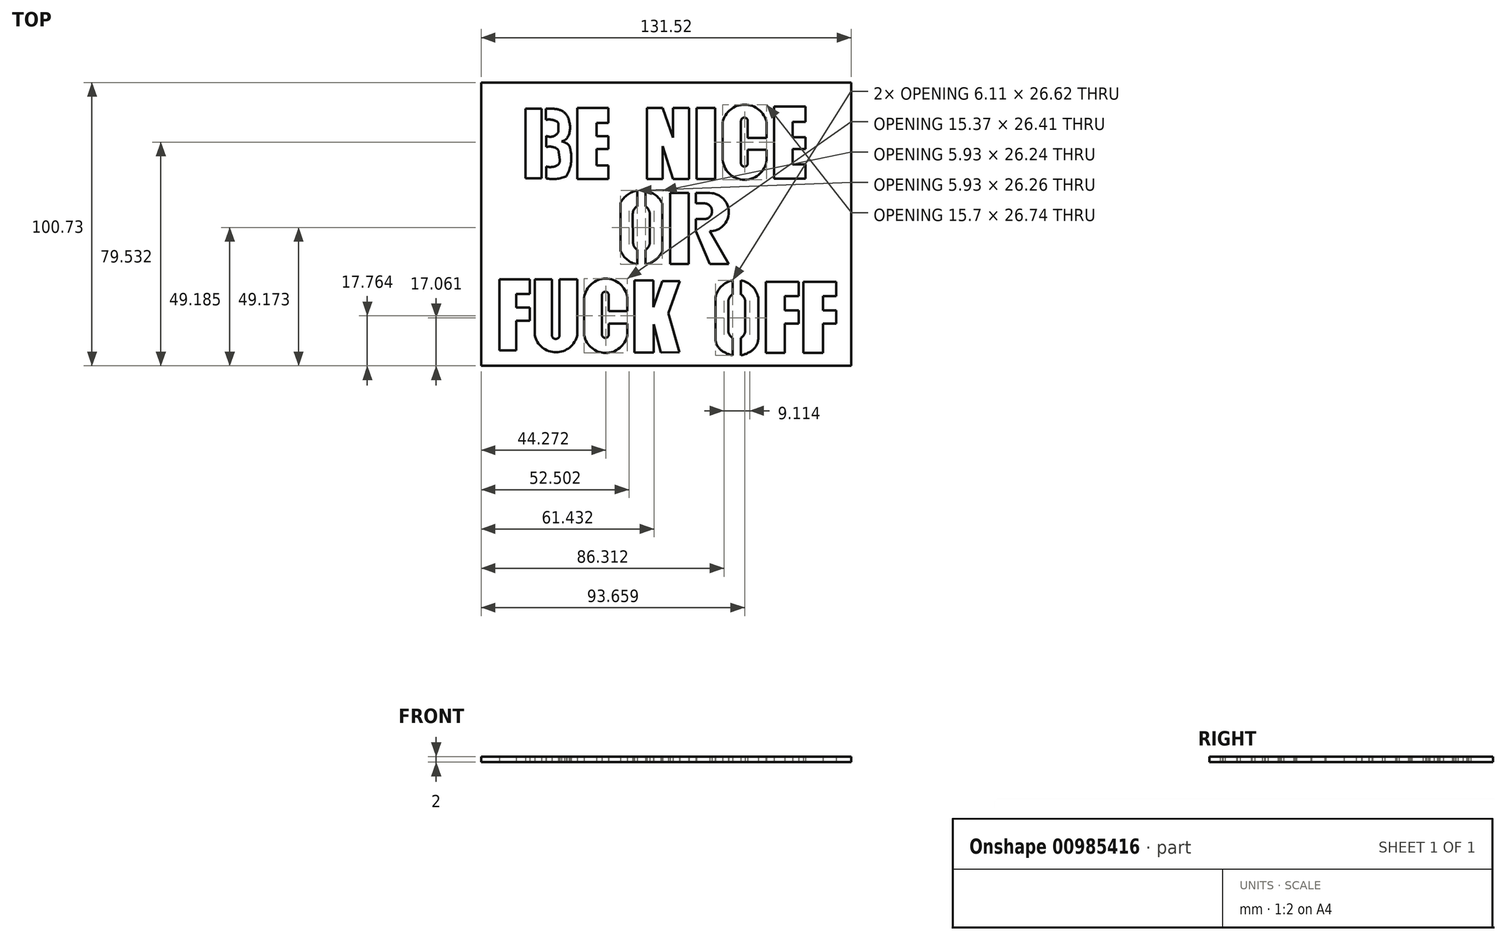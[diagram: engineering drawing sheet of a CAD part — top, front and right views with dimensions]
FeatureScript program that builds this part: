
annotation { "Feature Type Name" : "Feature", "Feature Type Description" : "" }
export const myFeature = defineFeature(function(context is Context, id is Id, definition is map)
    precondition{}
    {
        {
            var Q0;
            Q0=qCreatedBy(makeId("Top.planeOp"),FACE);
            var sketch = newSketch(context, id + "F0", { "sketchPlane" : qUnion([Q0])});
            skLineSegment(sketch, "E0", {"start": v(-58.34, 79.54) * mm, "end": v(-58.34, 83.48) * mm});
            skLineSegment(sketch, "E1", {"start": v(-58.22, 73.86) * mm, "end": v(-58.22, 69.88) * mm});
            skLineSegment(sketch, "E2", {"start": v(-58.22, 62.97) * mm, "end": v(-58.22, 58.7) * mm});
            skLineSegment(sketch, "E3", {"start": v(-58.34, 83.48) * mm, "end": v(-55.71, 83.48) * mm});
            skArc(sketch, "E4", {"start": v(-51.69, 82.15) * mm, "mid": v(-53.6, 83.14) * mm, "end": v(-55.71, 83.48) * mm});
            skArc(sketch, "E5", {"start": v(-50, 78.93) * mm, "mid": v(-50.58, 80.68) * mm, "end": v(-51.69, 82.15) * mm});
            skArc(sketch, "E6", {"start": v(-50.76, 73) * mm, "mid": v(-49.75, 75.89) * mm, "end": v(-50, 78.93) * mm});
            skArc(sketch, "E7", {"start": v(-52.7, 71.92) * mm, "mid": v(-51.63, 72.3) * mm, "end": v(-50.76, 73) * mm});
            skArc(sketch, "E8", {"start": v(-50, 70.42) * mm, "mid": v(-51.23, 71.38) * mm, "end": v(-52.7, 71.92) * mm});
            skArc(sketch, "E9", {"start": v(-49.42, 68) * mm, "mid": v(-49.63, 69.23) * mm, "end": v(-50, 70.42) * mm});
            skArc(sketch, "E10", {"start": v(-58.22, 58.7) * mm, "mid": v(-54.62, 58.57) * mm, "end": v(-51.12, 59.44) * mm});
            skArc(sketch, "E11", {"start": v(-51.12, 59.44) * mm, "mid": v(-49.47, 63.56) * mm, "end": v(-49.42, 68) * mm});
            skLineSegment(sketch, "E12", {"start": v(-47.15, 58.57) * mm, "end": v(-47.15, 83.76) * mm});
            skPoint(sketch, "E12.startSnap0", {"position": v(-54.62, 58.57) * mm});
            skLineSegment(sketch, "E13", {"start": v(-47.15, 83.76) * mm, "end": v(-36.04, 83.76) * mm});
            skLineSegment(sketch, "E14", {"start": v(-36.04, 83.76) * mm, "end": v(-36.04, 78.4) * mm});
            skLineSegment(sketch, "E15", {"start": v(-36.04, 78.4) * mm, "end": v(-40.33, 78.4) * mm});
            skLineSegment(sketch, "E16", {"start": v(-40.33, 78.4) * mm, "end": v(-40.33, 73.8) * mm});
            skLineSegment(sketch, "E17", {"start": v(-40.33, 73.8) * mm, "end": v(-36.04, 73.8) * mm});
            skLineSegment(sketch, "E18", {"start": v(-36.04, 73.8) * mm, "end": v(-36.04, 69.2) * mm});
            skLineSegment(sketch, "E19", {"start": v(-36.04, 69.2) * mm, "end": v(-40.33, 69.2) * mm});
            skLineSegment(sketch, "E20", {"start": v(-40.33, 69.2) * mm, "end": v(-40.33, 63.38) * mm});
            skLineSegment(sketch, "E21", {"start": v(-40.33, 63.38) * mm, "end": v(-36.04, 63.38) * mm});
            skLineSegment(sketch, "E22", {"start": v(-36.04, 63.38) * mm, "end": v(-36.04, 58.57) * mm});
            skLineSegment(sketch, "E23", {"start": v(-36.04, 58.57) * mm, "end": v(-47.15, 58.57) * mm});
            skLineSegment(sketch, "E24", {"start": v(-22.3, 58.57) * mm, "end": v(-22.3, 83.76) * mm});
            skLineSegment(sketch, "E25", {"start": v(-22.3, 83.76) * mm, "end": v(-16.73, 83.76) * mm});
            skLineSegment(sketch, "E26", {"start": v(-16.73, 83.76) * mm, "end": v(-13.1, 73.2) * mm});
            skLineSegment(sketch, "E27", {"start": v(-13.1, 73.2) * mm, "end": v(-13.1, 83.76) * mm});
            skLineSegment(sketch, "E28", {"start": v(-13.1, 83.76) * mm, "end": v(-7.43, 83.76) * mm});
            skLineSegment(sketch, "E29", {"start": v(-7.43, 83.76) * mm, "end": v(-7.43, 58.57) * mm});
            skLineSegment(sketch, "E30", {"start": v(-7.43, 58.57) * mm, "end": v(-13.1, 58.57) * mm});
            skLineSegment(sketch, "E31", {"start": v(-13.1, 58.57) * mm, "end": v(-16.73, 70.13) * mm});
            skLineSegment(sketch, "E32", {"start": v(-16.73, 70.13) * mm, "end": v(-16.73, 58.57) * mm});
            skLineSegment(sketch, "E33", {"start": v(-16.73, 58.57) * mm, "end": v(-22.3, 58.57) * mm});
            skLineSegment(sketch, "E34.bottom", {"start": v(-4.73, 83.76) * mm, "end": v(1.9, 83.76) * mm});
            skLineSegment(sketch, "E34.top", {"start": v(-4.73, 58.57) * mm, "end": v(1.9, 58.57) * mm});
            skLineSegment(sketch, "E34.left", {"start": v(-4.73, 83.76) * mm, "end": v(-4.73, 58.57) * mm});
            skLineSegment(sketch, "E34.right", {"start": v(1.9, 83.76) * mm, "end": v(1.9, 58.57) * mm});
            skLineSegment(sketch, "E35", {"start": v(4.53, 78.6) * mm, "end": v(4.53, 66.08) * mm});
            skLineSegment(sketch, "E36", {"start": v(11.08, 64.14) * mm, "end": v(11.08, 79.13) * mm});
            skLineSegment(sketch, "E37", {"start": v(13.5, 73.1) * mm, "end": v(13.5, 79.13) * mm});
            skLineSegment(sketch, "E38", {"start": v(13.5, 68.86) * mm, "end": v(13.5, 64.08) * mm});
            skArc(sketch, "E39", {"start": v(13.5, 79.13) * mm, "mid": v(12.3, 80.34) * mm, "end": v(11.08, 79.13) * mm});
            skArc(sketch, "E40", {"start": v(11.08, 64.14) * mm, "mid": v(12.26, 62.93) * mm, "end": v(13.5, 64.08) * mm});
            skLineSegment(sketch, "E41", {"start": v(13.5, 68.86) * mm, "end": v(20.23, 68.86) * mm});
            skLineSegment(sketch, "E42", {"start": v(13.5, 73.1) * mm, "end": v(20.23, 73.1) * mm});
            skLineSegment(sketch, "E43", {"start": v(20.23, 73.1) * mm, "end": v(20.23, 78.6) * mm});
            skLineSegment(sketch, "E44", {"start": v(20.23, 68.86) * mm, "end": v(20.23, 66.08) * mm});
            skArc(sketch, "E45", {"start": v(4.53, 66.08) * mm, "mid": v(12.38, 58.23) * mm, "end": v(20.23, 66.08) * mm});
            skArc(sketch, "E46", {"start": v(20.23, 78.6) * mm, "mid": v(12.38, 84.97) * mm, "end": v(4.53, 78.6) * mm});
            skLineSegment(sketch, "E47", {"start": v(22.87, 58.64) * mm, "end": v(22.87, 84.24) * mm});
            skLineSegment(sketch, "E48", {"start": v(22.87, 84.24) * mm, "end": v(34.02, 84.24) * mm});
            skLineSegment(sketch, "E49", {"start": v(34.02, 84.24) * mm, "end": v(34.02, 78.84) * mm});
            skLineSegment(sketch, "E50", {"start": v(34.02, 78.84) * mm, "end": v(29.45, 78.84) * mm});
            skLineSegment(sketch, "E51", {"start": v(29.45, 78.84) * mm, "end": v(29.45, 73.36) * mm});
            skLineSegment(sketch, "E52", {"start": v(29.45, 73.36) * mm, "end": v(34.02, 73.36) * mm});
            skLineSegment(sketch, "E53", {"start": v(34.02, 73.36) * mm, "end": v(34.02, 69.15) * mm});
            skLineSegment(sketch, "E54", {"start": v(34.02, 69.15) * mm, "end": v(29.45, 69.15) * mm});
            skLineSegment(sketch, "E55", {"start": v(29.45, 69.15) * mm, "end": v(29.45, 63.76) * mm});
            skLineSegment(sketch, "E56", {"start": v(29.45, 63.76) * mm, "end": v(34.02, 63.76) * mm});
            skLineSegment(sketch, "E57", {"start": v(34.02, 63.76) * mm, "end": v(34.02, 58.64) * mm});
            skLineSegment(sketch, "E58", {"start": v(34.02, 58.64) * mm, "end": v(22.87, 58.64) * mm});
            skArc(sketch, "E59", {"start": v(-16.88, 49.84) * mm, "mid": v(-19.32, 52.8) * mm, "end": v(-22.81, 54.36) * mm});
            skArc(sketch, "E60", {"start": v(-31.74, 33) * mm, "mid": v(-29.4, 29.8) * mm, "end": v(-25.81, 28.12) * mm});
            skLineSegment(sketch, "E61", {"start": v(-16.88, 33) * mm, "end": v(-16.88, 49.84) * mm});
            skLineSegment(sketch, "E62", {"start": v(-31.74, 50.12) * mm, "end": v(-31.74, 33) * mm});
            skArc(sketch, "E63.trimOffspring", {"start": v(-25.81, 54.39) * mm, "mid": v(-29.27, 52.93) * mm, "end": v(-31.74, 50.12) * mm});
            skArc(sketch, "E64.trimOffspring", {"start": v(-22.81, 28.12) * mm, "mid": v(-19.23, 29.8) * mm, "end": v(-16.88, 33) * mm});
            skLineSegment(sketch, "E65", {"start": v(-14.14, 53.5) * mm, "end": v(-14.14, 28.29) * mm});
            skLineSegment(sketch, "E66", {"start": v(-14.14, 28.29) * mm, "end": v(-7.48, 28.29) * mm});
            skLineSegment(sketch, "E67", {"start": v(-7.48, 28.29) * mm, "end": v(-7.48, 39.95) * mm});
            skPoint(sketch, "E68.orphan", {"position": v(-14.14, 54.5) * mm});
            skLineSegment(sketch, "E69", {"start": v(-7.48, 43.75) * mm, "end": v(-7.48, 49.61) * mm});
            skLineSegment(sketch, "E70", {"start": v(-7.48, 49.61) * mm, "end": v(-7.48, 53.5) * mm});
            skLineSegment(sketch, "E71.trimOffspring", {"start": v(-7.48, 53.5) * mm, "end": v(-14.14, 53.5) * mm});
            skLineSegment(sketch, "E72", {"start": v(-74.78, -2.43) * mm, "end": v(-74.78, 22.79) * mm});
            skLineSegment(sketch, "E73", {"start": v(-74.78, 22.79) * mm, "end": v(-63.97, 22.79) * mm});
            skLineSegment(sketch, "E74", {"start": v(-63.97, 22.79) * mm, "end": v(-63.97, 17.56) * mm});
            skLineSegment(sketch, "E75", {"start": v(-63.97, 17.56) * mm, "end": v(-68.85, 17.56) * mm});
            skLineSegment(sketch, "E76", {"start": v(-68.85, 17.56) * mm, "end": v(-68.85, 12.8) * mm});
            skLineSegment(sketch, "E77", {"start": v(-68.85, 12.8) * mm, "end": v(-64.06, 12.8) * mm});
            skLineSegment(sketch, "E78", {"start": v(-64.06, 12.8) * mm, "end": v(-64.06, 8.1) * mm});
            skLineSegment(sketch, "E79", {"start": v(-64.06, 8.1) * mm, "end": v(-68.85, 8.1) * mm});
            skLineSegment(sketch, "E80", {"start": v(-68.85, 8.1) * mm, "end": v(-68.85, -2.43) * mm});
            skLineSegment(sketch, "E81", {"start": v(-68.85, -2.43) * mm, "end": v(-74.78, -2.43) * mm});
            skLineSegment(sketch, "E82", {"start": v(-62.3, 22.76) * mm, "end": v(-56.19, 22.76) * mm});
            skLineSegment(sketch, "E83", {"start": v(-62.3, 22.76) * mm, "end": v(-62.3, 3) * mm});
            skLineSegment(sketch, "E84", {"start": v(-56.19, 22.76) * mm, "end": v(-56.19, 3) * mm});
            skLineSegment(sketch, "E85", {"start": v(-53.43, 22.76) * mm, "end": v(-53.43, 3) * mm});
            skLineSegment(sketch, "E86", {"start": v(-53.43, 22.76) * mm, "end": v(-47.1, 22.76) * mm});
            skLineSegment(sketch, "E87", {"start": v(-47.1, 22.76) * mm, "end": v(-47.1, 3) * mm});
            skArc(sketch, "E88", {"start": v(-56.19, 3) * mm, "mid": v(-54.8, 1.61) * mm, "end": v(-53.43, 3) * mm});
            skArc(sketch, "E89", {"start": v(-62.3, 3) * mm, "mid": v(-54.7, -3.12) * mm, "end": v(-47.1, 3) * mm});
            skLineSegment(sketch, "E90", {"start": v(-35.93, 11.56) * mm, "end": v(-29.34, 11.56) * mm});
            skLineSegment(sketch, "E91", {"start": v(-29.34, 7.1) * mm, "end": v(-35.93, 7.1) * mm});
            skLineSegment(sketch, "E92", {"start": v(-35.93, 7.1) * mm, "end": v(-35.93, 3.16) * mm});
            skLineSegment(sketch, "E93", {"start": v(-38.33, 3.16) * mm, "end": v(-38.33, 17.21) * mm});
            skLineSegment(sketch, "E94", {"start": v(-35.93, 11.56) * mm, "end": v(-35.93, 17.21) * mm});
            skArc(sketch, "E95", {"start": v(-35.93, 17.21) * mm, "mid": v(-37.13, 18.41) * mm, "end": v(-38.33, 17.21) * mm});
            skArc(sketch, "E96", {"start": v(-38.33, 3.16) * mm, "mid": v(-37.13, 1.96) * mm, "end": v(-35.93, 3.16) * mm});
            skLineSegment(sketch, "E97", {"start": v(-29.34, 7.1) * mm, "end": v(-29.34, 2.87) * mm});
            skLineSegment(sketch, "E98", {"start": v(-44.7, 2.87) * mm, "end": v(-44.7, 16.38) * mm});
            skArc(sketch, "E99", {"start": v(-29.32, 16.38) * mm, "mid": v(-37, 23.04) * mm, "end": v(-44.7, 16.38) * mm});
            skArc(sketch, "E100", {"start": v(-44.7, 2.87) * mm, "mid": v(-37.02, -3.37) * mm, "end": v(-29.34, 2.87) * mm});
            skLineSegment(sketch, "E101", {"start": v(-29.32, 16.38) * mm, "end": v(-29.34, 11.56) * mm});
            skLineSegment(sketch, "E102", {"start": v(-26.83, -3.2) * mm, "end": v(-26.83, 22.4) * mm});
            skLineSegment(sketch, "E103", {"start": v(-26.83, 22.4) * mm, "end": v(-20.13, 22.4) * mm});
            skLineSegment(sketch, "E104", {"start": v(-20.13, 22.4) * mm, "end": v(-20.13, 12.86) * mm});
            skLineSegment(sketch, "E105", {"start": v(-20.13, 12.86) * mm, "end": v(-16.95, 22.22) * mm});
            skLineSegment(sketch, "E106", {"start": v(-16.95, 22.22) * mm, "end": v(-10.68, 22.22) * mm});
            skLineSegment(sketch, "E107", {"start": v(-10.68, 22.22) * mm, "end": v(-14.8, 10.8) * mm});
            skLineSegment(sketch, "E108", {"start": v(-14.8, 10.8) * mm, "end": v(-10.77, -3.11) * mm});
            skLineSegment(sketch, "E109", {"start": v(-10.77, -3.11) * mm, "end": v(-17.47, -3.18) * mm});
            skLineSegment(sketch, "E110", {"start": v(-17.47, -3.18) * mm, "end": v(-19.96, 6.85) * mm});
            skLineSegment(sketch, "E111", {"start": v(-19.96, 6.85) * mm, "end": v(-19.96, -3.2) * mm});
            skLineSegment(sketch, "E112", {"start": v(-19.96, -3.2) * mm, "end": v(-26.83, -3.2) * mm});
            skArc(sketch, "E113", {"start": v(17.2, 16.36) * mm, "mid": v(15.07, 20.33) * mm, "end": v(11.09, 22.44) * mm});
            skArc(sketch, "E114", {"start": v(3.6, -2) * mm, "mid": v(5.7, -3.4) * mm, "end": v(8.09, -4.18) * mm});
            skLineSegment(sketch, "E115", {"start": v(17.2, 16.36) * mm, "end": v(17.2, 1.7) * mm});
            skLineSegment(sketch, "E116", {"start": v(1.98, 16.36) * mm, "end": v(1.98, 1.7) * mm});
            skArc(sketch, "E117.trimOffspring", {"start": v(8.09, 22.44) * mm, "mid": v(4.11, 20.33) * mm, "end": v(1.98, 16.36) * mm});
            skArc(sketch, "E118.trimOffspring", {"start": v(11.09, -4.18) * mm, "mid": v(13.49, -3.4) * mm, "end": v(15.57, -2) * mm});
            skLineSegment(sketch, "E119", {"start": v(19.94, -3.33) * mm, "end": v(19.94, 21.98) * mm});
            skLineSegment(sketch, "E120", {"start": v(19.94, 21.98) * mm, "end": v(31.6, 21.98) * mm});
            skLineSegment(sketch, "E121", {"start": v(31.6, 21.98) * mm, "end": v(31.6, 16.86) * mm});
            skLineSegment(sketch, "E122", {"start": v(31.6, 16.86) * mm, "end": v(26.69, 16.86) * mm});
            skLineSegment(sketch, "E123", {"start": v(26.69, 16.86) * mm, "end": v(26.69, 11.81) * mm});
            skLineSegment(sketch, "E124", {"start": v(26.69, 11.81) * mm, "end": v(31.6, 11.81) * mm});
            skLineSegment(sketch, "E125", {"start": v(31.6, 11.81) * mm, "end": v(31.6, 7.12) * mm});
            skLineSegment(sketch, "E126", {"start": v(31.6, 7.12) * mm, "end": v(26.69, 7.12) * mm});
            skLineSegment(sketch, "E127", {"start": v(26.69, 7.12) * mm, "end": v(26.69, -3.33) * mm});
            skLineSegment(sketch, "E128", {"start": v(26.69, -3.33) * mm, "end": v(19.94, -3.33) * mm});
            skLineSegment(sketch, "E129", {"start": v(33.23, -3.33) * mm, "end": v(33.23, 21.98) * mm});
            skLineSegment(sketch, "E130", {"start": v(33.23, 21.98) * mm, "end": v(44.96, 21.98) * mm});
            skLineSegment(sketch, "E131", {"start": v(44.96, 21.98) * mm, "end": v(44.96, 16.86) * mm});
            skLineSegment(sketch, "E132", {"start": v(44.96, 16.86) * mm, "end": v(40.2, 16.86) * mm});
            skLineSegment(sketch, "E133", {"start": v(40.2, 16.86) * mm, "end": v(40.2, 11.81) * mm});
            skLineSegment(sketch, "E134", {"start": v(40.2, 11.81) * mm, "end": v(44.96, 11.81) * mm});
            skLineSegment(sketch, "E135", {"start": v(44.96, 11.81) * mm, "end": v(44.96, 7.12) * mm});
            skLineSegment(sketch, "E136", {"start": v(44.96, 7.12) * mm, "end": v(40.2, 7.12) * mm});
            skLineSegment(sketch, "E137", {"start": v(40.2, 7.12) * mm, "end": v(40.2, -3.33) * mm});
            skLineSegment(sketch, "E138", {"start": v(40.2, -3.33) * mm, "end": v(33.23, -3.33) * mm});
            skLineSegment(sketch, "E139", {"start": v(9.59, 4.57) * mm, "end": v(9.59, 4.57) * mm});
            skArc(sketch, "E140", {"start": v(12.59, 14.82) * mm, "mid": v(12.19, 16.32) * mm, "end": v(11.09, 17.42) * mm});
            skArc(sketch, "E141", {"start": v(6.59, 4.57) * mm, "mid": v(7, 3.07) * mm, "end": v(8.09, 1.98) * mm});
            skLineSegment(sketch, "E142", {"start": v(6.59, 14.82) * mm, "end": v(6.59, 4.57) * mm});
            skLineSegment(sketch, "E143", {"start": v(12.59, 4.57) * mm, "end": v(12.59, 14.82) * mm});
            skPoint(sketch, "E144.visualSharp", {"position": v(1.98, 0) * mm});
            skArc(sketch, "E144.filletArc", {"start": v(1.98, 1.7) * mm, "mid": v(2.4, -0.32) * mm, "end": v(3.6, -2) * mm});
            skPoint(sketch, "E145.visualSharp", {"position": v(17.2, 0) * mm});
            skArc(sketch, "E145.filletArc", {"start": v(15.57, -2) * mm, "mid": v(16.78, -0.32) * mm, "end": v(17.2, 1.7) * mm});
            skLineSegment(sketch, "E146", {"start": v(8.09, -4.18) * mm, "end": v(8.09, 1.98) * mm});
            skLineSegment(sketch, "E147", {"start": v(11.09, -4.18) * mm, "end": v(11.09, 1.98) * mm});
            skArc(sketch, "E148.trimOffspring", {"start": v(8.09, 17.42) * mm, "mid": v(7, 16.32) * mm, "end": v(6.59, 14.82) * mm});
            skLineSegment(sketch, "E149.trimOffspring", {"start": v(8.09, 17.42) * mm, "end": v(8.09, 22.44) * mm});
            skLineSegment(sketch, "E150.trimOffspring", {"start": v(11.09, 17.42) * mm, "end": v(11.09, 22.44) * mm});
            skArc(sketch, "E151.trimOffspring", {"start": v(11.09, 1.98) * mm, "mid": v(12.19, 3.07) * mm, "end": v(12.59, 4.57) * mm});
            skArc(sketch, "E152", {"start": v(-21.38, 46.12) * mm, "mid": v(-21.76, 47.6) * mm, "end": v(-22.81, 48.71) * mm});
            skArc(sketch, "E153", {"start": v(-27.31, 36) * mm, "mid": v(-26.91, 34.5) * mm, "end": v(-25.81, 33.4) * mm});
            skLineSegment(sketch, "E154", {"start": v(-21.31, 36) * mm, "end": v(-21.38, 46.12) * mm});
            skLineSegment(sketch, "E155", {"start": v(-27.38, 46.18) * mm, "end": v(-27.31, 36) * mm});
            skLineSegment(sketch, "E156", {"start": v(-22.81, 28.12) * mm, "end": v(-22.81, 33.4) * mm});
            skLineSegment(sketch, "E157", {"start": v(-25.81, 28.12) * mm, "end": v(-25.81, 33.4) * mm});
            skArc(sketch, "E158.trimOffspring", {"start": v(-22.81, 33.4) * mm, "mid": v(-21.71, 34.5) * mm, "end": v(-21.31, 36) * mm});
            skLineSegment(sketch, "E159.trimOffspring", {"start": v(-22.81, 48.71) * mm, "end": v(-22.81, 54.36) * mm});
            skLineSegment(sketch, "E160.trimOffspring", {"start": v(-25.81, 48.79) * mm, "end": v(-25.81, 54.39) * mm});
            skArc(sketch, "E161.trimOffspring", {"start": v(-25.81, 48.79) * mm, "mid": v(-26.95, 47.7) * mm, "end": v(-27.38, 46.18) * mm});
            skLineSegment(sketch, "E162", {"start": v(-7.48, 39.95) * mm, "end": v(-7.48, 53.5) * mm});
            skLineSegment(sketch, "E163", {"start": v(-5.02, 53.5) * mm, "end": v(0, 53.5) * mm});
            skArc(sketch, "E164", {"start": v(0, 39.95) * mm, "mid": v(6.78, 46.72) * mm, "end": v(0, 53.5) * mm});
            skLineSegment(sketch, "E165", {"start": v(0, 39.95) * mm, "end": v(6.71, 28.29) * mm});
            skLineSegment(sketch, "E166", {"start": v(6.71, 28.29) * mm, "end": v(0, 28.29) * mm});
            skLineSegment(sketch, "E167", {"start": v(0, 28.29) * mm, "end": v(-5.02, 39.95) * mm});
            skLineSegment(sketch, "E168", {"start": v(-5.02, 39.95) * mm, "end": v(-5.02, 44.23) * mm});
            skLineSegment(sketch, "E169", {"start": v(-5.02, 49.84) * mm, "end": v(-2.02, 49.84) * mm});
            skLineSegment(sketch, "E170", {"start": v(-5.02, 44.23) * mm, "end": v(-2.02, 44.23) * mm});
            skArc(sketch, "E171", {"start": v(-2.02, 44.23) * mm, "mid": v(0.8, 47.04) * mm, "end": v(-2.02, 49.84) * mm});
            skLineSegment(sketch, "E172.trimOffspring", {"start": v(-5.02, 49.84) * mm, "end": v(-5.02, 53.5) * mm});
            skLineSegment(sketch, "E173", {"start": v(-81.28, -7.93) * mm, "end": v(-81.28, 92.8) * mm});
            skLineSegment(sketch, "E174", {"start": v(-81.28, -7.93) * mm, "end": v(50.24, -7.93) * mm});
            skLineSegment(sketch, "E175", {"start": v(50.24, -7.93) * mm, "end": v(50.24, 92.8) * mm});
            skLineSegment(sketch, "E176", {"start": v(50.24, 92.8) * mm, "end": v(-81.28, 92.8) * mm});
            skLineSegment(sketch, "E177", {"start": v(-37, 15.27) * mm, "end": v(-34.07, 15.27) * mm});
            skPoint(sketch, "E178.start.orphan", {"position": v(-59.21, 58.73) * mm});
            skArc(sketch, "E179", {"start": v(-54.35, 78.91) * mm, "mid": v(-56.29, 79.6) * mm, "end": v(-58.34, 79.54) * mm});
            skArc(sketch, "E180", {"start": v(-58.22, 73.86) * mm, "mid": v(-55.8, 73.67) * mm, "end": v(-53.88, 75.13) * mm});
            skLineSegment(sketch, "E181", {"start": v(-53.88, 75.13) * mm, "end": v(-53.88, 78.1) * mm});
            skArc(sketch, "E182", {"start": v(-54.8, 69.54) * mm, "mid": v(-56.48, 70) * mm, "end": v(-58.22, 69.88) * mm});
            skArc(sketch, "E183", {"start": v(-58.22, 62.97) * mm, "mid": v(-56.29, 62.76) * mm, "end": v(-54.42, 63.3) * mm});
            skLineSegment(sketch, "E184", {"start": v(-53.35, 65.32) * mm, "end": v(-53.67, 67.97) * mm});
            skPoint(sketch, "E185.visualSharp", {"position": v(-53.88, 78.6) * mm});
            skArc(sketch, "E185.filletArc", {"start": v(-53.88, 78.1) * mm, "mid": v(-54, 78.57) * mm, "end": v(-54.35, 78.91) * mm});
            skPoint(sketch, "E186.visualSharp", {"position": v(-53.21, 64.17) * mm});
            skArc(sketch, "E186.filletArc", {"start": v(-54.42, 63.3) * mm, "mid": v(-53.57, 64.14) * mm, "end": v(-53.35, 65.32) * mm});
            skPoint(sketch, "E187.visualSharp", {"position": v(-53.78, 68.9) * mm});
            skArc(sketch, "E187.filletArc", {"start": v(-53.67, 67.97) * mm, "mid": v(-54.03, 68.9) * mm, "end": v(-54.8, 69.54) * mm});
            skLineSegment(sketch, "E188", {"start": v(-60.37, 83.48) * mm, "end": v(-65.52, 83.48) * mm});
            skLineSegment(sketch, "E189", {"start": v(-65.52, 83.48) * mm, "end": v(-65.52, 58.73) * mm});
            skLineSegment(sketch, "E190", {"start": v(-65.52, 58.73) * mm, "end": v(-60.37, 58.73) * mm});
            skPoint(sketch, "E191.end.orphan", {"position": v(-64.54, 58.73) * mm});
            skPoint(sketch, "E191.start.orphan", {"position": v(-64.54, 83.48) * mm});
            skLineSegment(sketch, "E192", {"start": v(-59.83, 58.73) * mm, "end": v(-59.83, 83.48) * mm});
            skLineSegment(sketch, "E193", {"start": v(-59.83, 83.48) * mm, "end": v(-61.02, 83.48) * mm});
            skLineSegment(sketch, "E194", {"start": v(-59.83, 58.73) * mm, "end": v(-60.37, 58.73) * mm});
            skSolve(sketch);
        }
        {
            var Q0;
            Q0=makeQuery(id+"F0.imprint","IMPRINT",FACE,{"disambiguationData":[TD([[makeQuery(id+"F0.imprint","IMPRINT",EDGE,{"derivedFrom":sQuery(id+"F0.wireOp",EDGE,"E0")}),1.0]])]});
            extrude(context, id + "F1", {"entities" : qUnion([Q0]), "depth" : 2 * mm, "offsetDistance" : 25 * mm});
        }
    });
